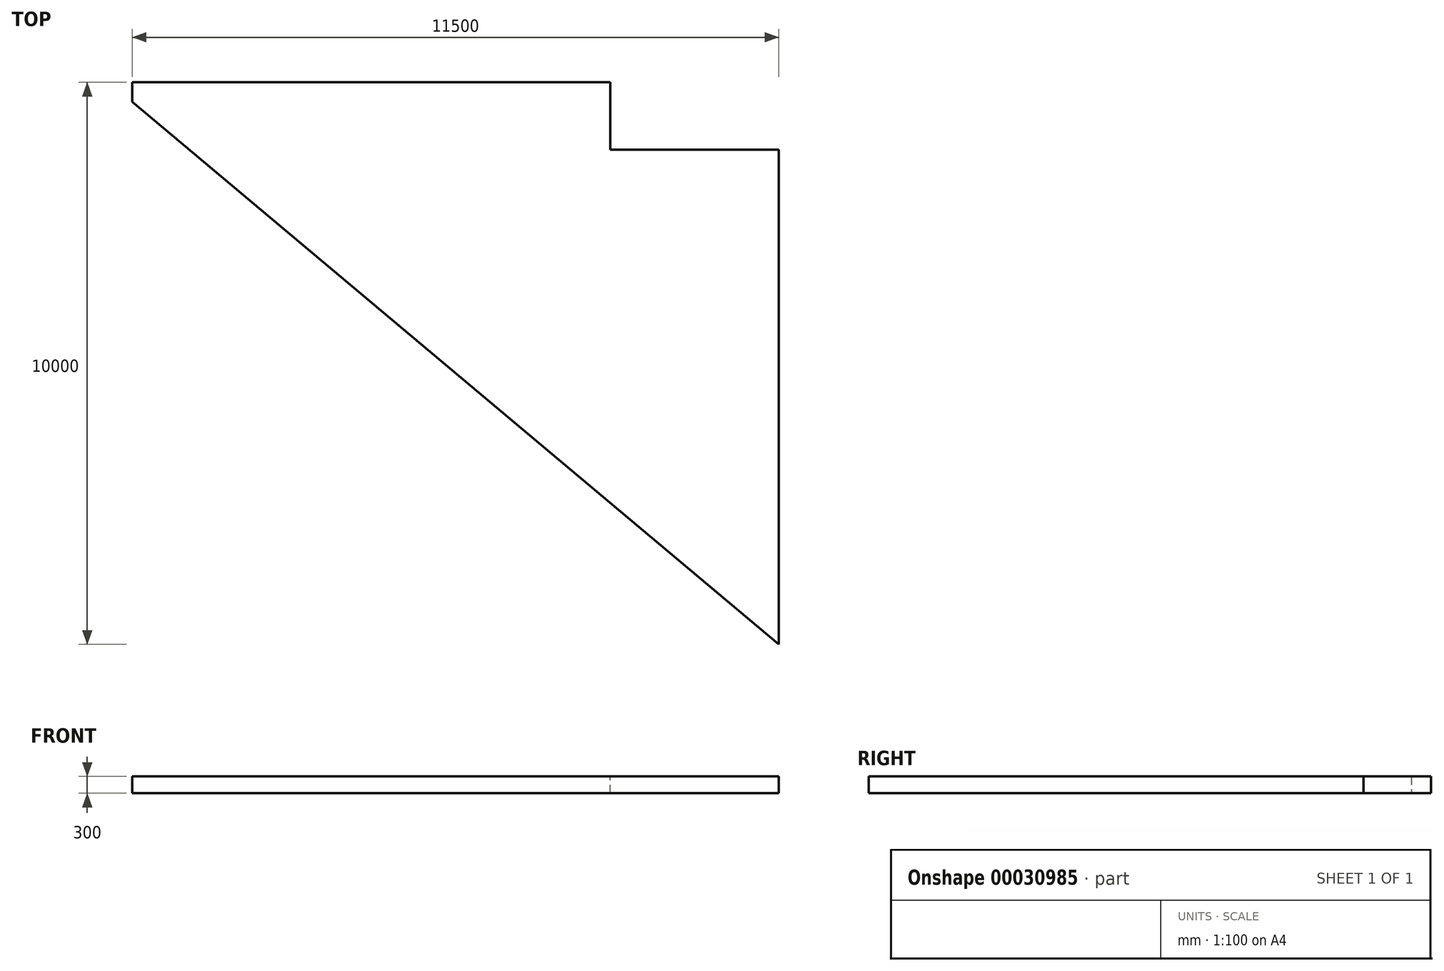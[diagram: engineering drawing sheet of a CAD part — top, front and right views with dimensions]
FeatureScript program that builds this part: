
annotation { "Feature Type Name" : "Feature", "Feature Type Description" : "" }
export const myFeature = defineFeature(function(context is Context, id is Id, definition is map)
    precondition{}
    {
        {
            var Q0;
            Q0=qCreatedBy(makeId("Top.planeOp"),FACE);
            var sketch = newSketch(context, id + "F0", { "sketchPlane" : qUnion([Q0])});
            skLineSegment(sketch, "E0", {"start": v(0, 0) * mm, "end": v(0, 350.35) * mm});
            skLineSegment(sketch, "E1", {"start": v(0, 350.35) * mm, "end": v(11500, 350.35) * mm});
            skLineSegment(sketch, "E2", {"start": v(11500, 350.35) * mm, "end": v(11500, -9649.65) * mm});
            skLineSegment(sketch, "E3", {"start": v(11500, -9649.65) * mm, "end": v(0, 0) * mm});
            skSolve(sketch);
        }
        {
            var Q0;
            Q0=makeQuery(id+"F0.imprint","IMPRINT",FACE,{"disambiguationData":[TD([[makeQuery(id+"F0.imprint","IMPRINT",EDGE,{"derivedFrom":sQuery(id+"F0.wireOp",EDGE,"E0")}),-1.0]])]});
            extrude(context, id + "F1", {"entities" : qUnion([Q0]), "depth" : 300 * mm});
        }
        {
            var Q0;
            Q0=makeQuery(id+"F1.opExtrude","CAP_FACE",FACE,{"disambiguationData":[OSD([sQuery(id+"F0.wireOp",EDGE,"E0"),sQuery(id+"F0.wireOp",EDGE,"E1"),sQuery(id+"F0.wireOp",EDGE,"E2"),sQuery(id+"F0.wireOp",EDGE,"E3")])],"isStart":false});
            var sketch = newSketch(context, id + "F2", { "sketchPlane" : qUnion([Q0])});
            skLineSegment(sketch, "E4.bottom", {"start": v(11500, 350.35) * mm, "end": v(8500, 350.35) * mm});
            skLineSegment(sketch, "E4.top", {"start": v(11500, -849.65) * mm, "end": v(8500, -849.65) * mm});
            skLineSegment(sketch, "E4.left", {"start": v(11500, 350.35) * mm, "end": v(11500, -849.65) * mm});
            skLineSegment(sketch, "E4.right", {"start": v(8500, 350.35) * mm, "end": v(8500, -849.65) * mm});
            skSolve(sketch);
        }
        {
            var Q0;
            Q0 = qSketchRegion(id + "F2", true);
            extrude(context, id + "F3", {"entities" : qUnion([Q0]), "operationType" : NewBodyOperationType.REMOVE, "endBound" : BoundingType.THROUGH_ALL, "oppositeDirection" : true, "depth" : 25 * mm});
        }
    });
